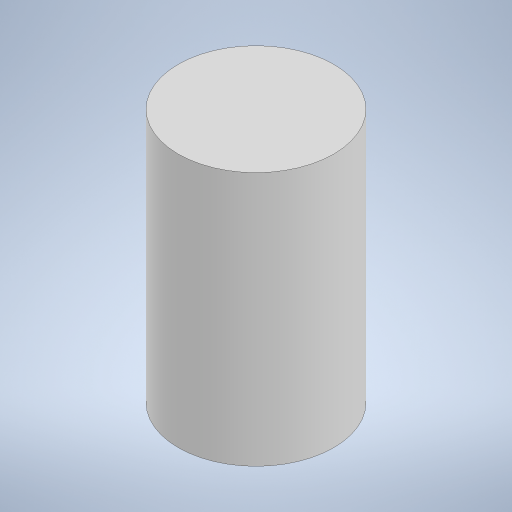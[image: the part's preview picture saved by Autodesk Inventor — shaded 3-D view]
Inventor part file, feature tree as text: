
AUTODESK INVENTOR PART (.ipt)
format: ipt  version: 2024 (Build 280153000, 153)  size: 199,168 bytes
history: native  units: in
note: dims shown in document units (in); Inventor stores cm internally (conversion verified against a paired STEP export)
features: extrude x2, other x1
ambient origin geometry x8: Origin, YZ Plane, XZ Plane, XY Plane, X Axis, Y Axis, Z Axis, Center Point
bodies: Body1 (feature_tree)
feature tree (3):
  other  "Sólido1"
  extrude  "Extrusión1"  Depth=0.7055in
  extrude  "Extrusión2"  Depth=0.8425in
